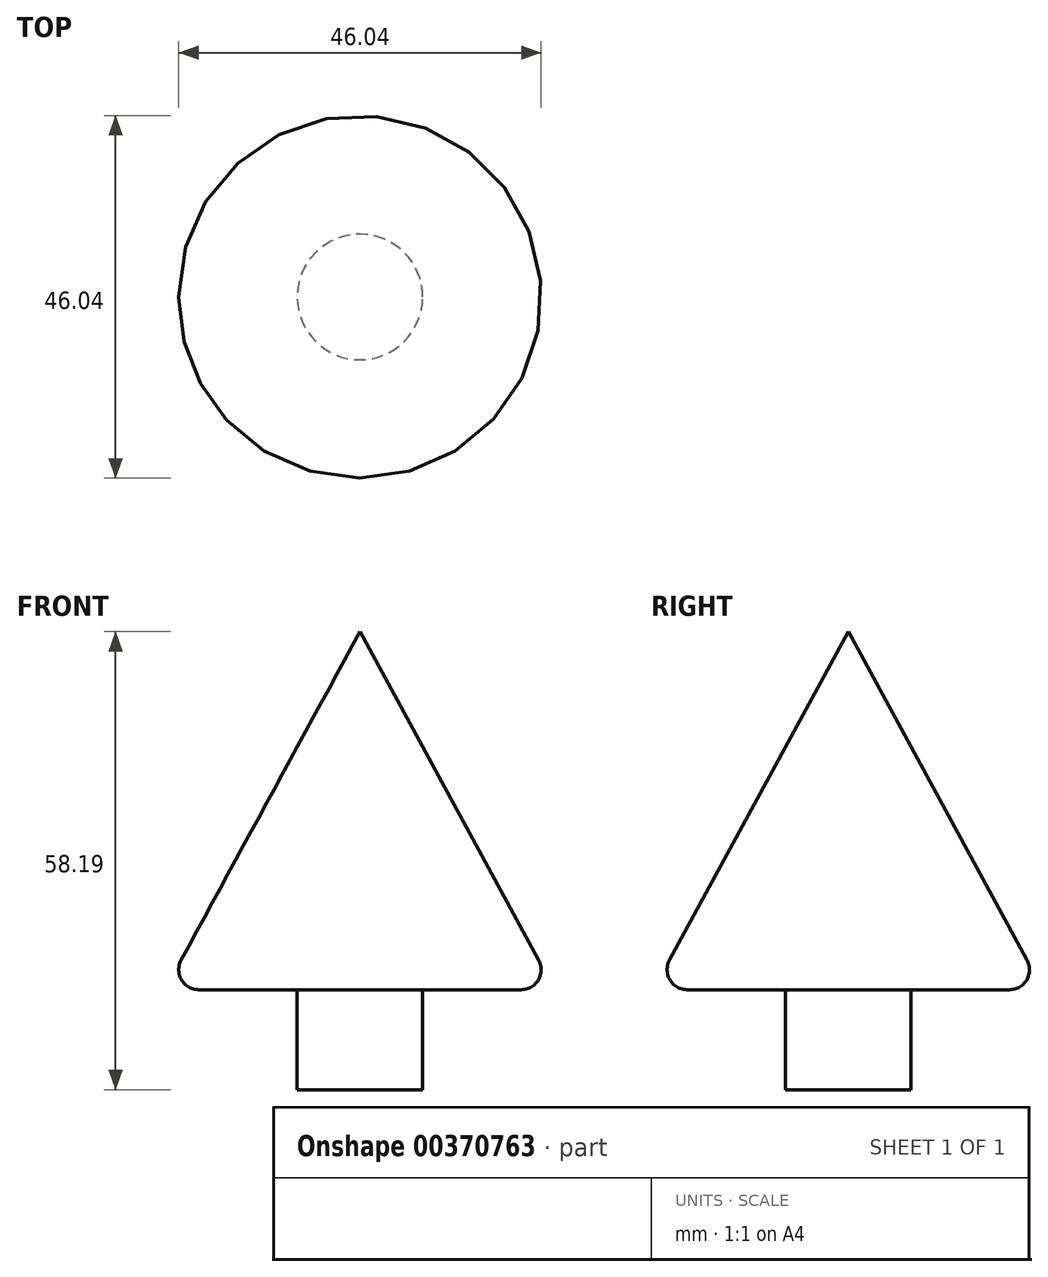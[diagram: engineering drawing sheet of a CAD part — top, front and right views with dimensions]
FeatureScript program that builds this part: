
annotation { "Feature Type Name" : "Feature", "Feature Type Description" : "" }
export const myFeature = defineFeature(function(context is Context, id is Id, definition is map)
    precondition{}
    {
        {
            var Q0;
            Q0=qCreatedBy(makeId("Front.planeOp"),FACE);
            var sketch = newSketch(context, id + "F0", { "sketchPlane" : qUnion([Q0])});
            skLineSegment(sketch, "E0", {"start": v(-18.32, -34.13) * mm, "end": v(-2.38, -34.13) * mm});
            skPoint(sketch, "E1.end.orphan", {"position": v(-19.16, -34.13) * mm});
            skLineSegment(sketch, "E2", {"start": v(-18.32, -21.43) * mm, "end": v(-18.32, -34.13) * mm});
            skLineSegment(sketch, "E3", {"start": v(-2.38, -34.13) * mm, "end": v(-2.38, -21.43) * mm});
            skLineSegment(sketch, "E4", {"start": v(-2.38, -21.43) * mm, "end": v(-18.32, -21.43) * mm});
            skPoint(sketch, "E5.endSnap0", {"position": v(-10.35, -21.43) * mm});
            skLineSegment(sketch, "E6", {"start": v(14.4, -21.43) * mm, "end": v(-34.27, -21.43) * mm});
            skLineSegment(sketch, "E7", {"start": v(-34.27, -21.43) * mm, "end": v(-10.35, 24.06) * mm});
            skLineSegment(sketch, "E8", {"start": v(14.4, -21.43) * mm, "end": v(-10.35, 24.06) * mm});
            skLineSegment(sketch, "E9", {"start": v(-10.35, 24.06) * mm, "end": v(-10.35, -46.97) * mm});
            skPoint(sketch, "E9.endSnap0", {"position": v(-10.35, -34.13) * mm});
            skSolve(sketch);
        }
        {
            var Q0;
            {var subQ0=sQuery(id+"F0.wireOp",EDGE,"E3");Q0=makeQuery(id+"F0.imprint","IMPRINT",FACE,{"disambiguationData":[TD([[makeQuery(id+"F0.imprint","IMPRINT",EDGE,{"derivedFrom":subQ0}),1.0]])]});}
            var Q1;
            {var subQ2=sQuery(id+"F0.wireOp",EDGE,"E8");Q1=makeQuery(id+"F0.imprint","IMPRINT",FACE,{"disambiguationData":[TD([[makeQuery(id+"F0.imprint","IMPRINT",EDGE,{"derivedFrom":subQ2}),1.0]])]});}
            var Q2;
            Q2=sQuery(id+"F0.wireOp",EDGE,"E9");
            revolve(context, id + "F1", {"entities" : qUnion([Q0, Q1]), "axis" : qUnion([Q2]), "revolveType" : RevolveType.FULL});
        }
        {
            var Q0;
            Q0=makeQuery(id+"F1.opRevolve","SWEPT_EDGE",EDGE,{"disambiguationData":[OSD([sQuery(id+"F0.wireOp",EDGE,"E6"),sQuery(id+"F0.wireOp",EDGE,"E8")])]});
            fillet(context, id + "F2", {"entities" : qUnion([Q0]), "radius" : 2.54 * mm, "tangentPropagation" : true, "allowEdgeOverflow" : false});
        }
    });
